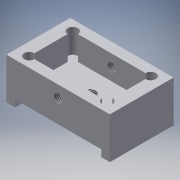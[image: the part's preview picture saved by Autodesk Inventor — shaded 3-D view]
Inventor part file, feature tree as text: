
AUTODESK INVENTOR PART (.ipt)
format: ipt  version: 2016 (Build 200138000, 138)  size: 148,992 bytes
history: native  units: mm
features: extrude x3, hole x3, sketch x1, projected_geometry x1
ambient origin geometry x8: Origin, YZ Plane, XZ Plane, XY Plane, X Axis, Y Axis, Z Axis, Center Point
bodies: Solid1 (feature_tree)
feature tree (8):
  extrude  "Extrusion1"  Depth=30.0mm
  hole  "Hole1"  [1 undecoded]
  hole  "Hole2"  [1 undecoded]
  extrude  "Extrusion2"  Depth=22.6mm
  hole  "Hole3"  [1 undecoded]
  extrude  "Extrusion3"  Depth=25.0mm
  sketch  "Sketch5"  dims[d0=18.5mm d1=30.0mm d2=12.0mm d3=0.0mm d4=3.242mm d5=8.0mm d6=4.0mm d7=2.0mm d8=90.0deg d9=11.8mm d10=20.594885mm d11=12.6mm d12=22.6mm d13=3.0mm d14=6.0mm d15=4.0mm d16=2.0mm d17=90.0deg d18=7.0mm d19=0.0mm d20=7.0mm d21=0.0mm d22=2.459mm d23=6.0mm d24=4.0mm d25=2.0mm d26=90.0deg d27=5.0mm d28=0.0mm d29=25.0mm d30=2.0mm d31=5.0mm d32=0.0mm d33=9.8mm]
  projected_geometry  "Projected Loop1"
note: 3 required parameter values undecoded (feature->parameter linkage not recoverable at this tier; creation-order binding heuristic only, values carry confidence <= 0.55)
